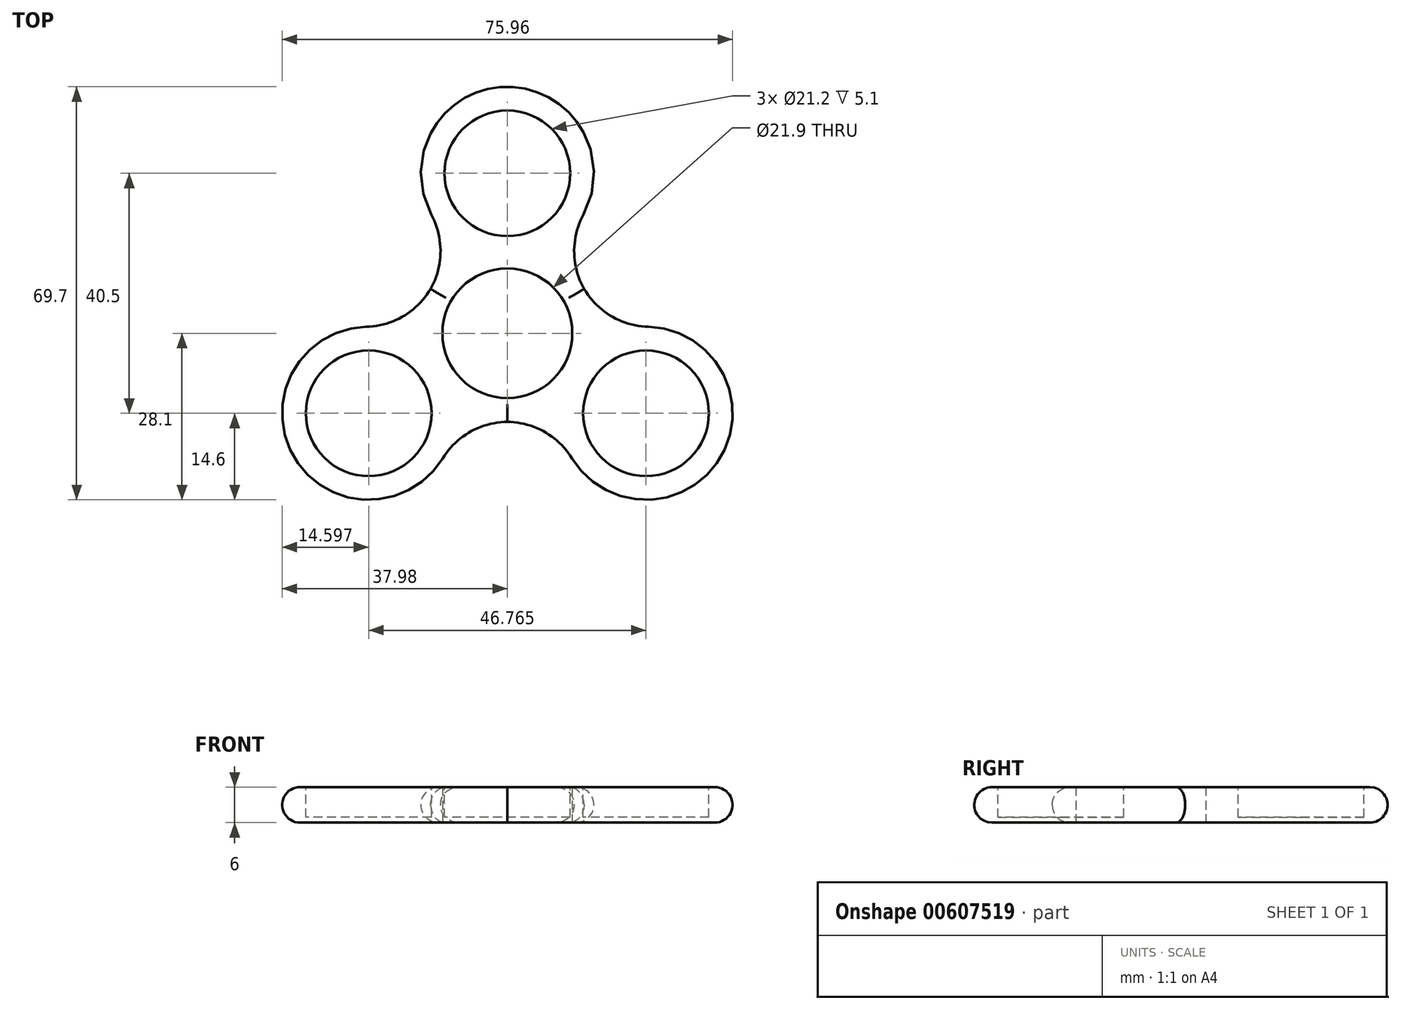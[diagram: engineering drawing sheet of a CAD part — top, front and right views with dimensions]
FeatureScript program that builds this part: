
annotation { "Feature Type Name" : "Feature", "Feature Type Description" : "" }
export const myFeature = defineFeature(function(context is Context, id is Id, definition is map)
    precondition{}
    {
        {
            var Q0;
            Q0=qCreatedBy(makeId("Top.planeOp"),FACE);
            var sketch = newSketch(context, id + "F0", { "sketchPlane" : qUnion([Q0])});
            skCircle(sketch, "E0", {"center": v(0, 0) * mm, "radius": 10.95 * mm});
            skCircle(sketch, "E1.cCircle", {"center": v(0, 0) * mm, "radius": 13.5 * mm, "construction": true});
            skLineSegment(sketch, "E1.0", {"start": v(-23.38, -13.5) * mm, "end": v(0, 27) * mm, "construction": true});
            skLineSegment(sketch, "E1.1", {"start": v(0, 27) * mm, "end": v(23.38, -13.5) * mm, "construction": true});
            skLineSegment(sketch, "E1.2", {"start": v(23.38, -13.5) * mm, "end": v(-23.38, -13.5) * mm, "construction": true});
            skPoint(sketch, "E1.0.midPoint", {"position": v(-11.7, 6.75) * mm});
            skCircle(sketch, "E2", {"center": v(0, 27) * mm, "radius": 10.6 * mm});
            skCircle(sketch, "E3", {"center": v(23.38, -13.5) * mm, "radius": 10.6 * mm});
            skCircle(sketch, "E4", {"center": v(-23.38, -13.5) * mm, "radius": 10.6 * mm});
            skCircle(sketch, "E5.0", {"center": v(-23.38, -13.5) * mm, "radius": 14.6 * mm});
            skCircle(sketch, "E6.0", {"center": v(23.38, -13.5) * mm, "radius": 14.6 * mm});
            skCircle(sketch, "E7.0", {"center": v(0, 27) * mm, "radius": 14.6 * mm});
            skCircle(sketch, "E8.0", {"center": v(0, 0) * mm, "radius": 14.95 * mm});
            skSolve(sketch);
        }
        {
            var Q0;
            Q0=qSketchRegion(id+"F0",true);
            var Q1;
            Q1=makeQuery(id+"F0.imprint","IMPRINT",FACE,{"disambiguationData":[TD([[makeQuery(id+"F0.imprint","IMPRINT",EDGE,{"derivedFrom":sQuery(id+"F0.wireOp",EDGE,"E4")}),1.0]])]});
            var Q2;
            Q2=makeQuery(id+"F0.imprint","IMPRINT",FACE,{"disambiguationData":[TD([[makeQuery(id+"F0.imprint","IMPRINT",EDGE,{"derivedFrom":sQuery(id+"F0.wireOp",EDGE,"E2")}),1.0]])]});
            var Q3;
            Q3=makeQuery(id+"F0.imprint","IMPRINT",FACE,{"disambiguationData":[TD([[makeQuery(id+"F0.imprint","IMPRINT",EDGE,{"derivedFrom":sQuery(id+"F0.wireOp",EDGE,"E3")}),1.0]])]});
            extrude(context, id + "F1", {"entities" : qUnion([Q0, Q1, Q2, Q3]), "depth" : 6 * mm, "offsetDistance" : 25 * mm});
        }
        {
            var Q0;
            {var subQ0=sQuery(id+"F0.wireOp",EDGE,"E8.0");var subQ1=sQuery(id+"F0.wireOp",EDGE,"E5.0");Q0=makeQuery(id+"F1.opExtrude","SWEPT_EDGE",EDGE,{"disambiguationData":[OSD([subQ1,subQ0]),TDD([makeQuery(id+"F0.imprint","INTERSECT",VERTEX,{"disambiguationData":[OD(1.0)],"derivedFrom":[subQ1,subQ0]})])]});}
            var Q1;
            {var subQ0=sQuery(id+"F0.wireOp",EDGE,"E8.0");var subQ1=sQuery(id+"F0.wireOp",EDGE,"E6.0");Q1=makeQuery(id+"F1.opExtrude","SWEPT_EDGE",EDGE,{"disambiguationData":[OSD([subQ1,subQ0]),TDD([makeQuery(id+"F0.imprint","INTERSECT",VERTEX,{"disambiguationData":[OD(0.0)],"derivedFrom":[subQ1,subQ0]})])]});}
            var Q2;
            {var subQ0=sQuery(id+"F0.wireOp",EDGE,"E8.0");var subQ1=sQuery(id+"F0.wireOp",EDGE,"E7.0");Q2=makeQuery(id+"F1.opExtrude","SWEPT_EDGE",EDGE,{"disambiguationData":[OSD([subQ1,subQ0]),TDD([makeQuery(id+"F0.imprint","INTERSECT",VERTEX,{"disambiguationData":[OD(1.0)],"derivedFrom":[subQ1,subQ0]})])]});}
            var Q3;
            {var subQ0=sQuery(id+"F0.wireOp",EDGE,"E8.0");var subQ1=sQuery(id+"F0.wireOp",EDGE,"E6.0");Q3=makeQuery(id+"F1.opExtrude","SWEPT_EDGE",EDGE,{"disambiguationData":[OSD([subQ1,subQ0]),TDD([makeQuery(id+"F0.imprint","INTERSECT",VERTEX,{"disambiguationData":[OD(1.0)],"derivedFrom":[subQ1,subQ0]})])]});}
            var Q4;
            {var subQ0=sQuery(id+"F0.wireOp",EDGE,"E8.0");var subQ1=sQuery(id+"F0.wireOp",EDGE,"E7.0");Q4=makeQuery(id+"F1.opExtrude","SWEPT_EDGE",EDGE,{"disambiguationData":[OSD([subQ1,subQ0]),TDD([makeQuery(id+"F0.imprint","INTERSECT",VERTEX,{"disambiguationData":[OD(0.0)],"derivedFrom":[subQ1,subQ0]})])]});}
            var Q5;
            {var subQ0=sQuery(id+"F0.wireOp",EDGE,"E8.0");var subQ1=sQuery(id+"F0.wireOp",EDGE,"E5.0");Q5=makeQuery(id+"F1.opExtrude","SWEPT_EDGE",EDGE,{"disambiguationData":[OSD([subQ1,subQ0]),TDD([makeQuery(id+"F0.imprint","INTERSECT",VERTEX,{"disambiguationData":[OD(0.0)],"derivedFrom":[subQ1,subQ0]})])]});}
            fillet(context, id + "F2", {"entities" : qUnion([Q0, Q1, Q2, Q3, Q4, Q5]), "radius" : 13 * mm, "tangentPropagation" : true, "allowEdgeOverflow" : false});
        }
        {
            var Q0;
            Q0=makeQuery(id+"F1.opExtrude","CAP_EDGE",EDGE,{"disambiguationData":[OSD([sQuery(id+"F0.wireOp",EDGE,"E7.0")])],"isStart":false});
            var Q1;
            Q1=makeQuery(id+"F1.opExtrude","CAP_EDGE",EDGE,{"disambiguationData":[OSD([sQuery(id+"F0.wireOp",EDGE,"E7.0")])],"isStart":true});
            var Q2;
            Q2=makeQuery(id+"F1.opExtrude","CAP_EDGE",EDGE,{"disambiguationData":[OSD([sQuery(id+"F0.wireOp",EDGE,"E5.0")])],"isStart":false});
            var Q3;
            Q3=makeQuery(id+"F1.opExtrude","CAP_EDGE",EDGE,{"disambiguationData":[OSD([sQuery(id+"F0.wireOp",EDGE,"E5.0")])],"isStart":true});
            var Q4;
            Q4=makeQuery(id+"F1.opExtrude","CAP_EDGE",EDGE,{"disambiguationData":[OSD([sQuery(id+"F0.wireOp",EDGE,"E6.0")])],"isStart":false});
            var Q5;
            Q5=makeQuery(id+"F1.opExtrude","CAP_EDGE",EDGE,{"disambiguationData":[OSD([sQuery(id+"F0.wireOp",EDGE,"E6.0")])],"isStart":true});
            fillet(context, id + "F3", {"entities" : qUnion([Q0, Q1, Q2, Q3, Q4, Q5]), "radius" : 3 * mm, "tangentPropagation" : true, "allowEdgeOverflow" : false});
        }
        {
            var Q0;
            Q0=makeQuery(id+"F1.opExtrude","CAP_FACE",FACE,{"disambiguationData":[OSD([sQuery(id+"F0.wireOp",EDGE,"E0"),sQuery(id+"F0.wireOp",EDGE,"E5.0"),sQuery(id+"F0.wireOp",EDGE,"E6.0"),sQuery(id+"F0.wireOp",EDGE,"E7.0"),sQuery(id+"F0.wireOp",EDGE,"E8.0")])],"isStart":false});
            var sketch = newSketch(context, id + "F4", { "sketchPlane" : qUnion([Q0])});
            skCircle(sketch, "E9", {"center": v(0, 27) * mm, "radius": 10.6 * mm});
            skCircle(sketch, "E10", {"center": v(-23.38, -13.5) * mm, "radius": 10.6 * mm});
            skCircle(sketch, "E11", {"center": v(23.38, -13.5) * mm, "radius": 10.6 * mm});
            skSolve(sketch);
        }
        {
            var Q0;
            Q0 = qSketchRegion(id + "F4", true);
            extrude(context, id + "F5", {"entities" : qUnion([Q0]), "operationType" : NewBodyOperationType.REMOVE, "oppositeDirection" : true, "depth" : 5.1 * mm, "offsetDistance" : 25 * mm});
        }
    });
